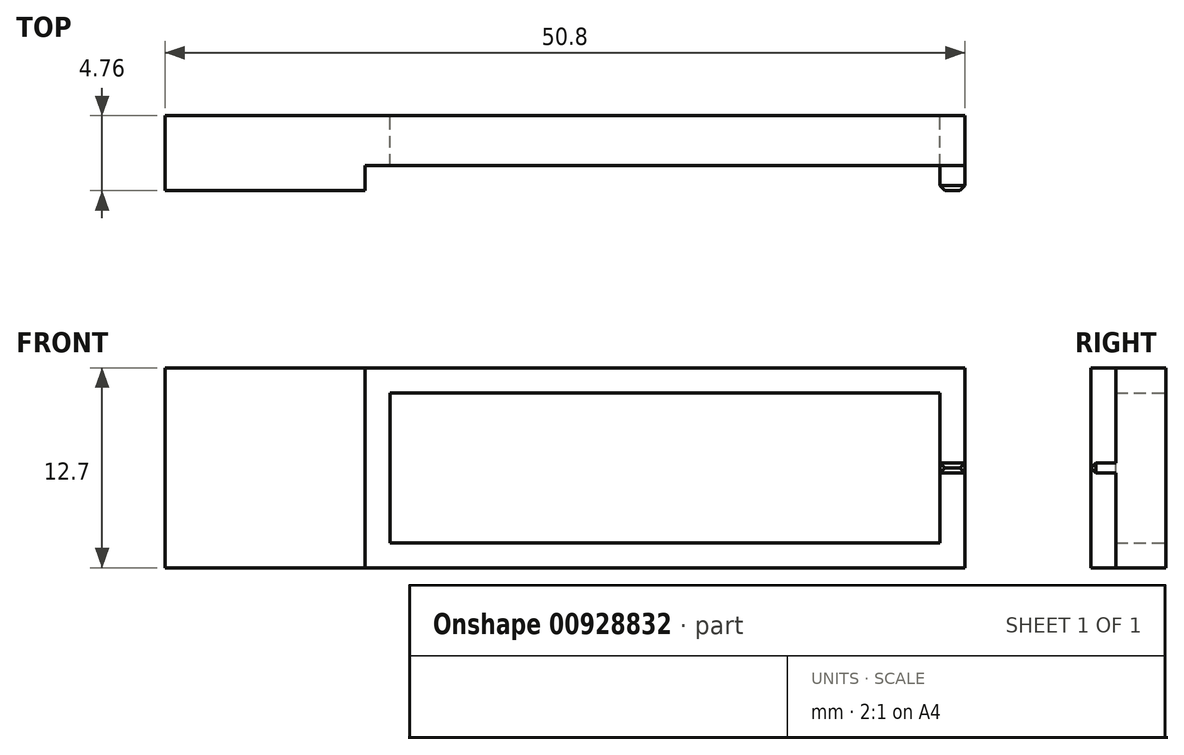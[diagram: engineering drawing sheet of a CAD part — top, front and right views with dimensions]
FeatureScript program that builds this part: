
annotation { "Feature Type Name" : "Feature", "Feature Type Description" : "" }
export const myFeature = defineFeature(function(context is Context, id is Id, definition is map)
    precondition{}
    {
        {
            var Q0;
            Q0=qCreatedBy(makeId("Front.planeOp"),FACE);
            var sketch = newSketch(context, id + "F0", { "sketchPlane" : qUnion([Q0])});
            skLineSegment(sketch, "E0", {"start": v(0, 0) * mm, "end": v(50.8, 0) * mm, "construction": true});
            skLineSegment(sketch, "E1", {"start": v(0, 0) * mm, "end": v(0, 50.8) * mm, "construction": true});
            skLineSegment(sketch, "E2.bottom", {"start": v(6.35, -6.35) * mm, "end": v(-6.35, -6.35) * mm});
            skLineSegment(sketch, "E2.top", {"start": v(6.35, 6.35) * mm, "end": v(-6.35, 6.35) * mm});
            skLineSegment(sketch, "E2.left", {"start": v(6.35, -6.35) * mm, "end": v(6.35, 6.35) * mm});
            skLineSegment(sketch, "E2.right", {"start": v(-6.35, -6.35) * mm, "end": v(-6.35, 6.35) * mm});
            skPoint(sketch, "E2.middle", {"position": v(0, 0) * mm});
            skSolve(sketch);
        }
        {
            var Q0;
            Q0=makeQuery(id+"F0.imprint","IMPRINT",FACE,{"disambiguationData":[TD([[makeQuery(id+"F0.imprint","IMPRINT",EDGE,{"derivedFrom":sQuery(id+"F0.wireOp",EDGE,"E2.bottom")}),-1.0]])]});
            extrude(context, id + "F1", {"entities" : qUnion([Q0]), "depth" : 4.76 * mm, "offsetDistance" : 25.4 * mm});
        }
        {
            var Q0;
            Q0=qCreatedBy(makeId("Front.planeOp"),FACE);
            var sketch = newSketch(context, id + "F2", { "sketchPlane" : qUnion([Q0])});
            skLineSegment(sketch, "E3", {"start": v(0, 0) * mm, "end": v(50.8, 0) * mm, "construction": true});
            skLineSegment(sketch, "E4", {"start": v(0, 0) * mm, "end": v(0, 50.8) * mm, "construction": true});
            skLineSegment(sketch, "E5.bottom", {"start": v(6.35, -6.35) * mm, "end": v(-6.35, -6.35) * mm});
            skLineSegment(sketch, "E5.top", {"start": v(6.35, 6.35) * mm, "end": v(-6.35, 6.35) * mm});
            skLineSegment(sketch, "E5.left", {"start": v(6.35, -6.35) * mm, "end": v(6.35, 6.35) * mm});
            skLineSegment(sketch, "E5.right", {"start": v(-6.35, -6.35) * mm, "end": v(-6.35, 6.35) * mm});
            skPoint(sketch, "E5.middle", {"position": v(0, 0) * mm});
            skLineSegment(sketch, "E6.bottom", {"start": v(6.35, -6.35) * mm, "end": v(44.45, -6.35) * mm});
            skLineSegment(sketch, "E6.top", {"start": v(6.35, 6.35) * mm, "end": v(44.45, 6.35) * mm});
            skLineSegment(sketch, "E6.right", {"start": v(44.45, -6.35) * mm, "end": v(44.45, 6.35) * mm});
            skLineSegment(sketch, "E7.0", {"start": v(7.94, -4.76) * mm, "end": v(7.94, 4.76) * mm});
            skLineSegment(sketch, "E7.1", {"start": v(7.94, -4.76) * mm, "end": v(42.86, -4.76) * mm});
            skLineSegment(sketch, "E7.2", {"start": v(42.86, -4.76) * mm, "end": v(42.86, 4.76) * mm});
            skLineSegment(sketch, "E7.3", {"start": v(7.94, 4.76) * mm, "end": v(42.86, 4.76) * mm});
            skSolve(sketch);
        }
        {
            var Q0;
            Q0=makeQuery(id+"F2.imprint","IMPRINT",FACE,{"disambiguationData":[TD([[makeQuery(id+"F2.imprint","IMPRINT",EDGE,{"derivedFrom":sQuery(id+"F2.wireOp",EDGE,"E6.bottom")}),1.0]])]});
            extrude(context, id + "F3", {"entities" : qUnion([Q0]), "operationType" : NewBodyOperationType.ADD, "depth" : 3.17 * mm, "offsetDistance" : 25.4 * mm});
        }
        {
            var Q0;
            Q0=makeQuery(id+"F3.opExtrude","CAP_FACE",FACE,{"disambiguationData":[OSD([sQuery(id+"F2.wireOp",EDGE,"E6.bottom"),sQuery(id+"F2.wireOp",EDGE,"E6.top"),sQuery(id+"F2.wireOp",EDGE,"E5.left"),sQuery(id+"F2.wireOp",EDGE,"E6.right"),sQuery(id+"F2.wireOp",EDGE,"E7.0"),sQuery(id+"F2.wireOp",EDGE,"E7.1"),sQuery(id+"F2.wireOp",EDGE,"E7.2"),sQuery(id+"F2.wireOp",EDGE,"E7.3")])],"isStart":false});
            var sketch = newSketch(context, id + "F4", { "sketchPlane" : qUnion([Q0])});
            skLineSegment(sketch, "E8", {"start": v(0, 0) * mm, "end": v(49.07, 0) * mm, "construction": true});
            skLineSegment(sketch, "E9.0", {"start": v(0, -0.32) * mm, "end": v(49.07, -0.32) * mm, "construction": true});
            skLineSegment(sketch, "E10.0", {"start": v(0, 0.32) * mm, "end": v(49.07, 0.32) * mm, "construction": true});
            skLineSegment(sketch, "E11.0", {"start": v(42.86, -4.76) * mm, "end": v(42.86, 4.76) * mm, "construction": true});
            skLineSegment(sketch, "E12.0", {"start": v(44.45, -6.35) * mm, "end": v(44.45, 6.35) * mm, "construction": true});
            skLineSegment(sketch, "E13.bottom", {"start": v(42.86, 0.32) * mm, "end": v(44.45, 0.32) * mm});
            skLineSegment(sketch, "E13.top", {"start": v(42.86, -0.32) * mm, "end": v(44.45, -0.32) * mm});
            skLineSegment(sketch, "E13.left", {"start": v(42.86, 0.32) * mm, "end": v(42.86, -0.32) * mm});
            skLineSegment(sketch, "E13.right", {"start": v(44.45, 0.32) * mm, "end": v(44.45, -0.32) * mm});
            skSolve(sketch);
        }
        {
            var Q0;
            Q0=makeQuery(id+"F4.imprint","IMPRINT",FACE,{"disambiguationData":[TD([[makeQuery(id+"F4.imprint","IMPRINT",EDGE,{"derivedFrom":sQuery(id+"F4.wireOp",EDGE,"E13.bottom")}),-1.0]])]});
            extrude(context, id + "F5", {"entities" : qUnion([Q0]), "operationType" : NewBodyOperationType.ADD, "depth" : 1.59 * mm, "offsetDistance" : 25.4 * mm});
        }
        {
            var Q0;
            Q0=makeQuery(id+"F5.opExtrude","CAP_FACE",FACE,{"disambiguationData":[OSD([sQuery(id+"F4.wireOp",EDGE,"E13.bottom"),sQuery(id+"F4.wireOp",EDGE,"E13.top"),sQuery(id+"F4.wireOp",EDGE,"E13.left"),sQuery(id+"F4.wireOp",EDGE,"E13.right")])],"isStart":false});
            chamfer(context, id + "F6", {"entities" : qUnion([Q0]), "width" : 0.32 * mm, "tangentPropagation" : true});
        }
    });
